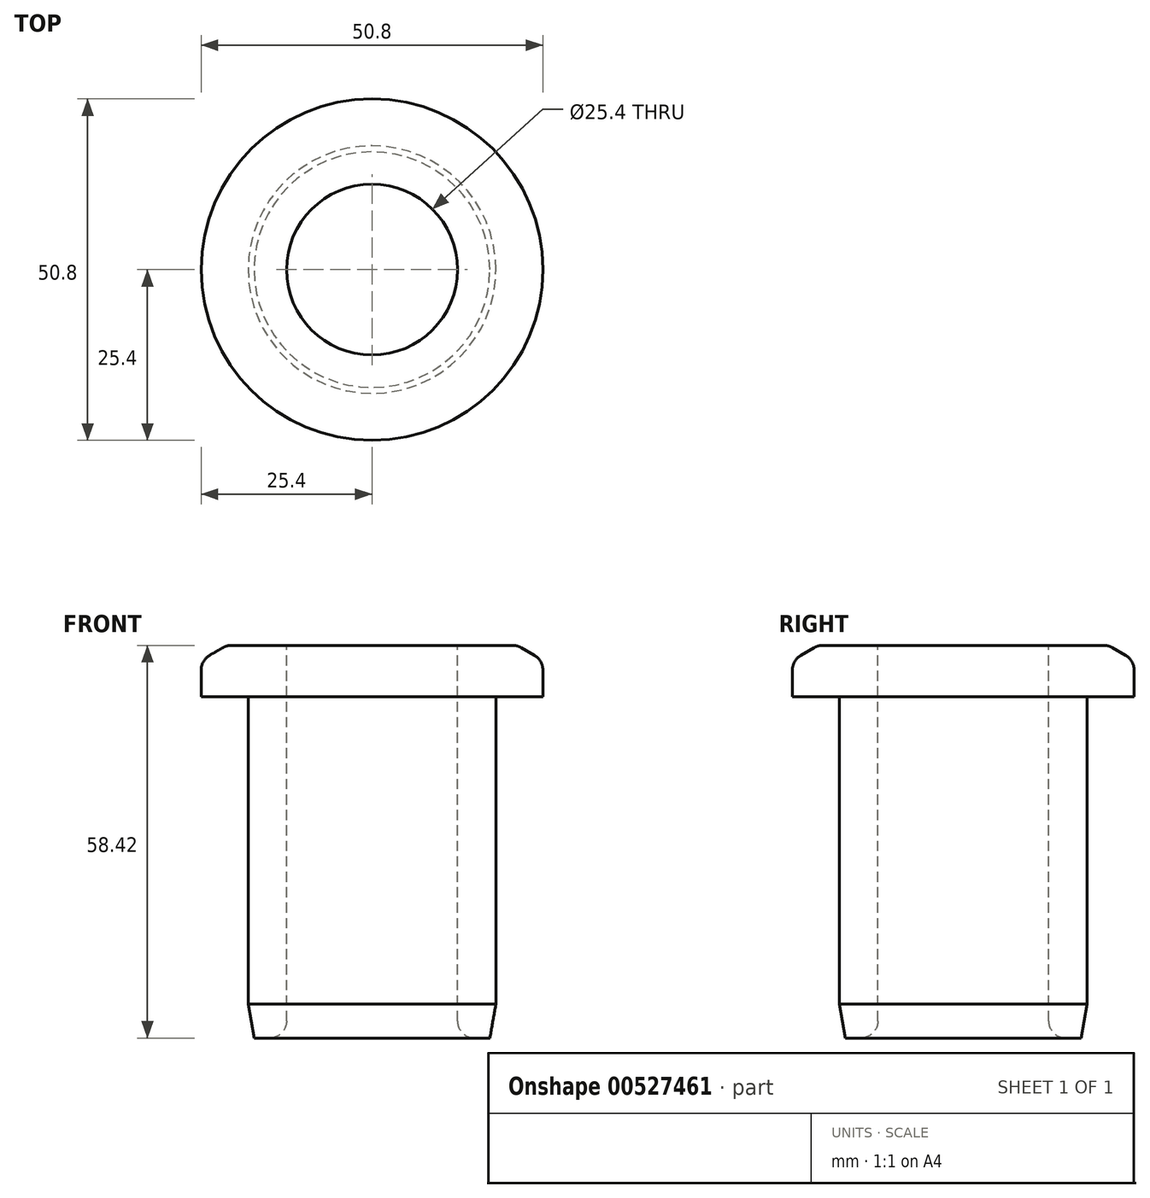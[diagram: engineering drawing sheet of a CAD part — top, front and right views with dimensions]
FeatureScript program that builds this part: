
annotation { "Feature Type Name" : "Feature", "Feature Type Description" : "" }
export const myFeature = defineFeature(function(context is Context, id is Id, definition is map)
    precondition{}
    {
        {
            var Q0;
            Q0=qCreatedBy(makeId("Top.planeOp"),FACE);
            var sketch = newSketch(context, id + "F0", { "sketchPlane" : qUnion([Q0])});
            skCircle(sketch, "E0", {"center": v(0, 0) * mm, "radius": 18.41 * mm});
            skSolve(sketch);
        }
        {
            var Q0;
            Q0=makeQuery(id+"F0.imprint","IMPRINT",FACE,{"disambiguationData":[TD([[makeQuery(id+"F0.imprint","IMPRINT",EDGE,{"derivedFrom":sQuery(id+"F0.wireOp",EDGE,"E0")}),1.0]])]});
            extrude(context, id + "F1", {"entities" : qUnion([Q0]), "depth" : 50.8 * mm, "offsetDistance" : 25.4 * mm});
        }
        {
            var Q0;
            Q0=makeQuery(id+"F1.opExtrude","CAP_FACE",FACE,{"disambiguationData":[OSD([sQuery(id+"F0.wireOp",EDGE,"E0")])],"isStart":false});
            var sketch = newSketch(context, id + "F2", { "sketchPlane" : qUnion([Q0])});
            skCircle(sketch, "E1", {"center": v(0, 0) * mm, "radius": 25.4 * mm});
            skSolve(sketch);
        }
        {
            var Q0;
            Q0=makeQuery(id+"F2.imprint","IMPRINT",FACE,{"disambiguationData":[TD([[makeQuery(id+"F2.imprint","IMPRINT",EDGE,{"derivedFrom":sQuery(id+"F2.wireOp",EDGE,"E1")}),1.0]])]});
            var Q1;
            Q1=makeQuery(id+"F2.imprint","IMPRINT",FACE,{"disambiguationData":[TD([[makeQuery(id+"F2.imprint","IMPRINT",EDGE,{"derivedFrom":makeQuery(id+"F1.opExtrude","CAP_EDGE",EDGE,{"disambiguationData":[OSD([sQuery(id+"F0.wireOp",EDGE,"E0")])],"isStart":false})}),1.0]])]});
            extrude(context, id + "F3", {"entities" : qUnion([Q0, Q1]), "operationType" : NewBodyOperationType.ADD, "depth" : 7.62 * mm, "offsetDistance" : 25.4 * mm});
        }
        {
            var Q0;
            Q0=makeQuery(id+"F3.opExtrude","CAP_FACE",FACE,{"disambiguationData":[OSD([sQuery(id+"F2.wireOp",EDGE,"E1")])],"isStart":false});
            var sketch = newSketch(context, id + "F4", { "sketchPlane" : qUnion([Q0])});
            skCircle(sketch, "E2", {"center": v(0, 0) * mm, "radius": 12.7 * mm});
            skSolve(sketch);
        }
        {
            var Q0;
            Q0=makeQuery(id+"F4.imprint","IMPRINT",FACE,{"disambiguationData":[TD([[makeQuery(id+"F4.imprint","IMPRINT",EDGE,{"derivedFrom":sQuery(id+"F4.wireOp",EDGE,"E2")}),1.0]])]});
            extrude(context, id + "F5", {"entities" : qUnion([Q0]), "operationType" : NewBodyOperationType.REMOVE, "endBound" : BoundingType.THROUGH_ALL, "oppositeDirection" : true, "depth" : 25.4 * mm, "offsetDistance" : 25.4 * mm});
        }
        {
            var Q0;
            Q0=makeQuery(id+"F3.opExtrude","CAP_EDGE",EDGE,{"disambiguationData":[OSD([sQuery(id+"F2.wireOp",EDGE,"E1")])],"isStart":false});
            var Q1;
            Q1=makeQuery(id+"F5.boolean.opBoolean","COPY",EDGE,{"derivedFrom":makeQuery(id+"F5.opExtrude","CAP_EDGE",EDGE,{"disambiguationData":[OSD([sQuery(id+"F4.wireOp",EDGE,"E2")])],"isStart":true})});
            chamfer(context, id + "F6", {"entities" : qUnion([Q0, Q1]), "chamferType" : ChamferType.OFFSET_ANGLE, "width" : 3.8 * mm, "oppositeDirection" : false, "angle" : 30 * degree, "tangentPropagation" : true});
        }
        {
            var Q0;
            Q0=makeQuery(id+"F6.opChamfer","BLEND_EDGE",EDGE,{"blendedFrom":[makeQuery(id+"F5.boolean.opBoolean","COPY",EDGE,{"derivedFrom":makeQuery(id+"F5.opExtrude","CAP_EDGE",EDGE,{"disambiguationData":[OSD([sQuery(id+"F4.wireOp",EDGE,"E2")])],"isStart":true})}),makeQuery(id+"F3.opExtrude","CAP_FACE",FACE,{"disambiguationData":[OSD([sQuery(id+"F2.wireOp",EDGE,"E1")])],"isStart":false})],"blendedInto":[makeQuery(id+"F3.opExtrude","CAP_FACE",FACE,{"disambiguationData":[OSD([sQuery(id+"F2.wireOp",EDGE,"E1")])],"isStart":false})]});
            var Q1;
            {var subQ0=sQuery(id+"F2.wireOp",EDGE,"E1");Q1=makeQuery(id+"F6.opChamfer","BLEND_EDGE",EDGE,{"blendedFrom":[makeQuery(id+"F3.opExtrude","CAP_EDGE",EDGE,{"disambiguationData":[OSD([subQ0])],"isStart":false}),makeQuery(id+"F3.opExtrude","CAP_FACE",FACE,{"disambiguationData":[OSD([subQ0])],"isStart":false})],"blendedInto":[makeQuery(id+"F3.opExtrude","CAP_FACE",FACE,{"disambiguationData":[OSD([subQ0])],"isStart":false})]});}
            var Q2;
            {var subQ0=sQuery(id+"F2.wireOp",EDGE,"E1");Q2=makeQuery(id+"F6.opChamfer","BLEND_EDGE",EDGE,{"blendedFrom":[makeQuery(id+"F3.opExtrude","CAP_EDGE",EDGE,{"disambiguationData":[OSD([subQ0])],"isStart":false}),makeQuery(id+"F3.opExtrude","SWEPT_FACE",FACE,{"disambiguationData":[OSD([subQ0])]})],"blendedInto":[makeQuery(id+"F3.opExtrude","SWEPT_FACE",FACE,{"disambiguationData":[OSD([subQ0])]})]});}
            var Q3;
            {var subQ0=sQuery(id+"F4.wireOp",EDGE,"E2");Q3=makeQuery(id+"F6.opChamfer","BLEND_EDGE",EDGE,{"blendedFrom":[makeQuery(id+"F5.boolean.opBoolean","COPY",EDGE,{"derivedFrom":makeQuery(id+"F5.opExtrude","CAP_EDGE",EDGE,{"disambiguationData":[OSD([subQ0])],"isStart":true})}),makeQuery(id+"F5.boolean.opBoolean","COPY",FACE,{"derivedFrom":makeQuery(id+"F5.opExtrude","SWEPT_FACE",FACE,{"disambiguationData":[OSD([subQ0])]})})],"blendedInto":[makeQuery(id+"F5.boolean.opBoolean","COPY",FACE,{"derivedFrom":makeQuery(id+"F5.opExtrude","SWEPT_FACE",FACE,{"disambiguationData":[OSD([subQ0])]})})]});}
            fillet(context, id + "F7", {"entities" : qUnion([Q0, Q1, Q2, Q3]), "radius" : 2.54 * mm, "tangentPropagation" : true, "allowEdgeOverflow" : false});
        }
        {
            var Q0;
            Q0=makeQuery(id+"F5.boolean.opBoolean","INTERSECT",EDGE,{"derivedFrom":[makeQuery(id+"F1.opExtrude","CAP_FACE",FACE,{"disambiguationData":[OSD([sQuery(id+"F0.wireOp",EDGE,"E0")])],"isStart":true}),makeQuery(id+"F5.opExtrude","SWEPT_FACE",FACE,{"disambiguationData":[OSD([sQuery(id+"F4.wireOp",EDGE,"E2")])]})]});
            fillet(context, id + "F8", {"entities" : qUnion([Q0]), "radius" : 2.54 * mm, "tangentPropagation" : true, "allowEdgeOverflow" : false});
        }
        {
            var Q0;
            Q0=makeQuery(id+"F1.opExtrude","CAP_EDGE",EDGE,{"disambiguationData":[OSD([sQuery(id+"F0.wireOp",EDGE,"E0")])],"isStart":true});
            chamfer(context, id + "F9", {"entities" : qUnion([Q0]), "chamferType" : ChamferType.OFFSET_ANGLE, "width" : 5.08 * mm, "oppositeDirection" : false, "angle" : 10 * degree, "tangentPropagation" : true});
        }
    });
